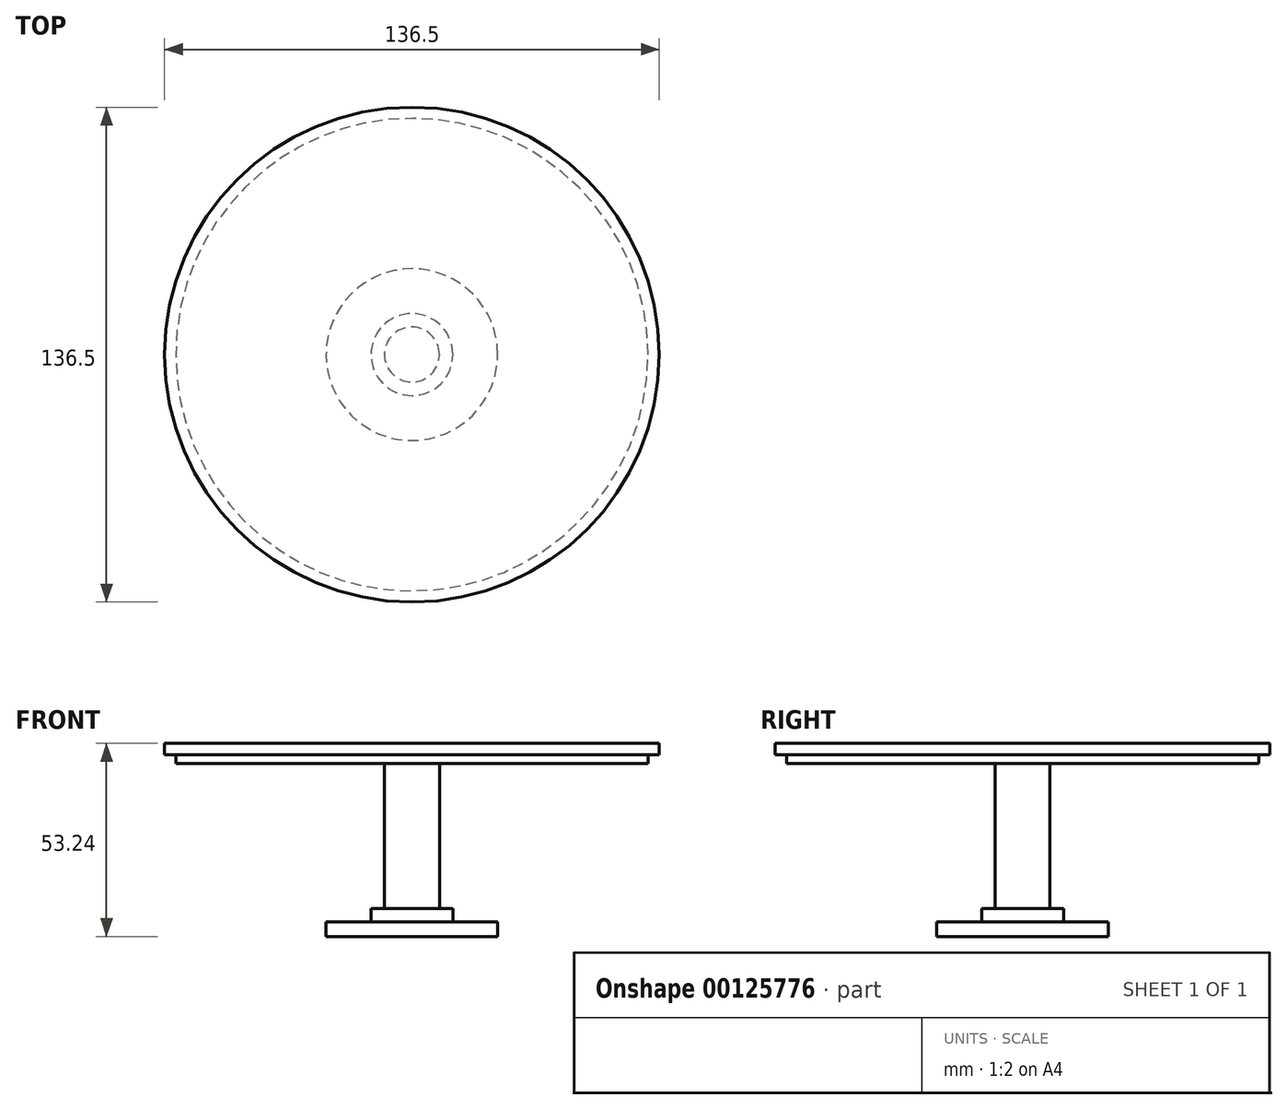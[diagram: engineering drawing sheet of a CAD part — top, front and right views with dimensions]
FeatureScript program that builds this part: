
annotation { "Feature Type Name" : "Feature", "Feature Type Description" : "" }
export const myFeature = defineFeature(function(context is Context, id is Id, definition is map)
    precondition{}
    {
        {
            var Q0;
            Q0=qCreatedBy(makeId("Front.planeOp"),FACE);
            var sketch = newSketch(context, id + "F0", { "sketchPlane" : qUnion([Q0])});
            skLineSegment(sketch, "E0", {"start": v(0, 56.8) * mm, "end": v(-68.25, 56.8) * mm});
            skLineSegment(sketch, "E1", {"start": v(-68.25, 56.8) * mm, "end": v(-68.25, 53.7) * mm});
            skLineSegment(sketch, "E2", {"start": v(-68.25, 53.7) * mm, "end": v(-65.15, 53.7) * mm});
            skLineSegment(sketch, "E3", {"start": v(-65.15, 53.7) * mm, "end": v(-65.15, 51.22) * mm});
            skLineSegment(sketch, "E4", {"start": v(-65.15, 51.22) * mm, "end": v(-7.58, 51.22) * mm});
            skLineSegment(sketch, "E5", {"start": v(-7.58, 51.22) * mm, "end": v(-7.58, 11.3) * mm});
            skLineSegment(sketch, "E6", {"start": v(-7.58, 11.3) * mm, "end": v(-11.3, 11.3) * mm});
            skLineSegment(sketch, "E7", {"start": v(-11.3, 11.3) * mm, "end": v(-11.3, 7.58) * mm});
            skLineSegment(sketch, "E8", {"start": v(-11.3, 7.58) * mm, "end": v(-23.68, 7.58) * mm});
            skLineSegment(sketch, "E9", {"start": v(-23.68, 7.58) * mm, "end": v(-23.68, 3.56) * mm});
            skLineSegment(sketch, "E10", {"start": v(-23.68, 3.56) * mm, "end": v(0, 3.56) * mm});
            skLineSegment(sketch, "E11", {"start": v(0, 3.56) * mm, "end": v(0, 56.8) * mm});
            skSolve(sketch);
        }
        {
            var Q0;
            Q0 = qSketchRegion(id + "F0", true);
            var Q1;
            Q1=sQuery(id+"F0.wireOp",EDGE,"E11");
            revolve(context, id + "F1", {"entities" : qUnion([Q0]), "axis" : qUnion([Q1]), "revolveType" : RevolveType.FULL});
        }
    });
